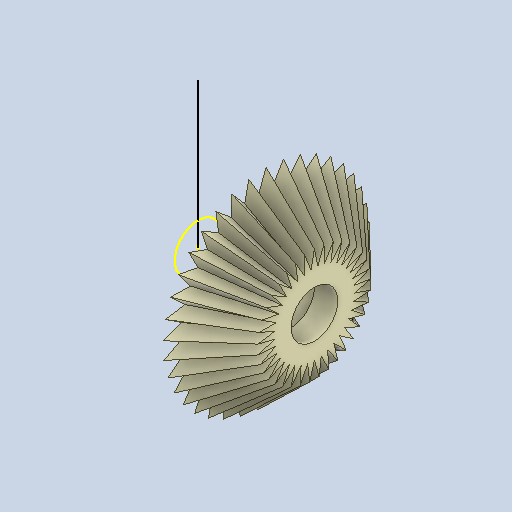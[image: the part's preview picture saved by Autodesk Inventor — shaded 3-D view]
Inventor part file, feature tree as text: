
AUTODESK INVENTOR PART (.ipt)
format: ipt  version: 2023 (Build 270158030, 158C)  size: 586,752 bytes
history: native  units: in
note: dims shown in document units (in); Inventor stores cm internally (conversion verified against a paired STEP export)
features: sketch x7, extrude x4, other x2, pattern_circular x2, loft x1
ambient origin geometry x8: Origin, YZ Plane, XZ Plane, XY Plane, X Axis, Y Axis, Z Axis, Center Point
bodies: Solid1 (feature_tree)
feature tree (16):
  other  "Main Body"
  extrude  "Teeth"  TaperAngle=45.0deg  [1 undecoded]
  pattern_circular  "Circular Pattern1"  Count=5  [1 undecoded]
  loft  "Angle Teeth"
  pattern_circular  "Circular Pattern2"  Count=2  [1 undecoded]
  extrude  "Extrusion4"  TaperAngle=0.0deg  [1 undecoded]
  sketch  "Sketch13"  dims[d22=14.5669in d23=360.0deg d25=0.0in d26=90.0deg]
  extrude  "Extrusion5"  Depth=14.5669in TaperAngle=360.0deg
  extrude  "Extrusion6"  TaperAngle=0.0deg  [1 undecoded]
  sketch  "Sketch1"  dims[d0=0.7874in d1=45.0deg]
  sketch  "Sketch6"  dims[d2=0.5906in d3=1.9685in]
  sketch  "Sketch11"  dims[d4=90.0deg d18=45.0deg]
  other  "Edges2"
  sketch  "Sketch12"  dims[d19=0.3937in d20=0.7874in d21=0.0in]
  sketch  "Sketch14"  dims[d27=0.0in d28=90.0deg d29=14.5669in d30=360.0deg]
  sketch  "Sketch15"  dims[d32=0.5906in d33=0.0in d34=0.0in d35=0.8661in d36=0.0in d37=1.0236in d38=0.315in d39=0.0in]
note: 5 required parameter values undecoded (feature->parameter linkage not recoverable at this tier; creation-order binding heuristic only, values carry confidence <= 0.55)
